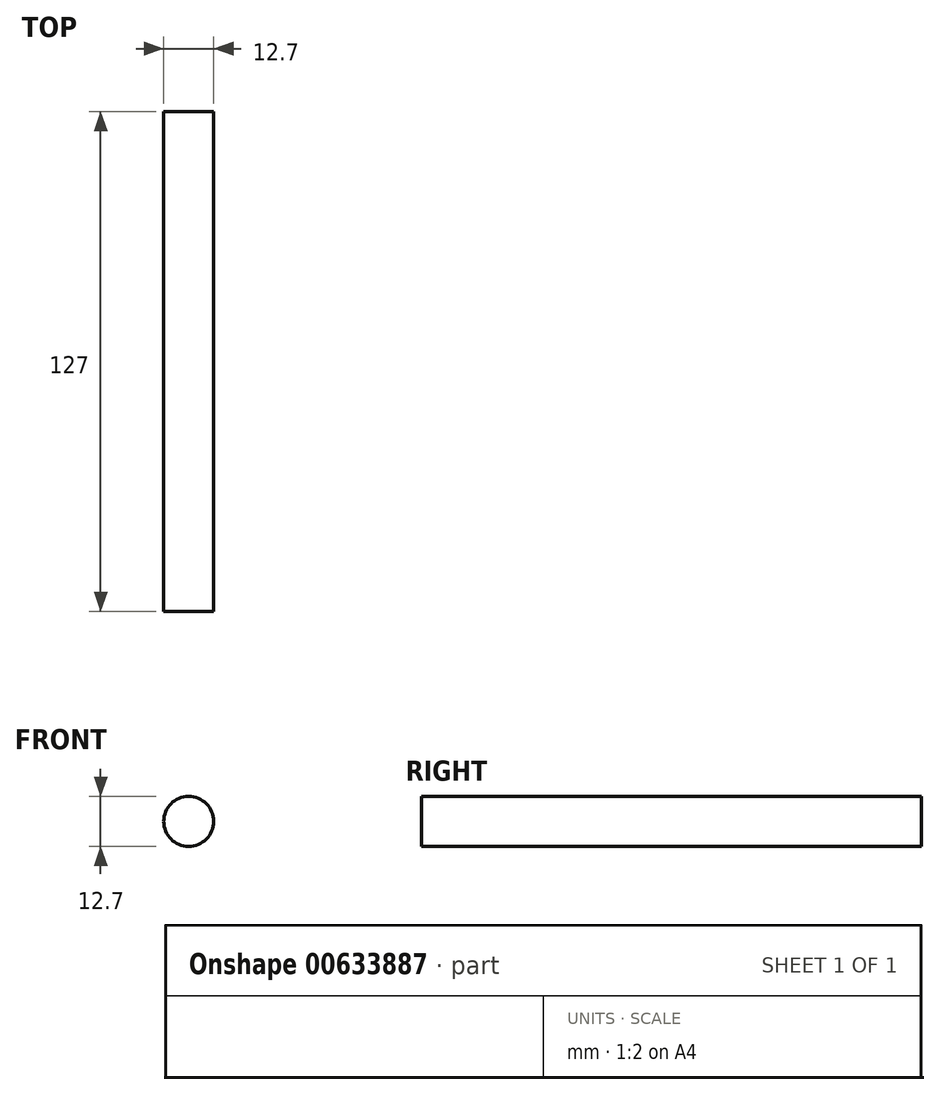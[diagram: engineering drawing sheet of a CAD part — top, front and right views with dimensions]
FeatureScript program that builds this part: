
annotation { "Feature Type Name" : "Feature", "Feature Type Description" : "" }
export const myFeature = defineFeature(function(context is Context, id is Id, definition is map)
    precondition{}
    {
        {
            var Q0;
            Q0=qCreatedBy(makeId("Front.planeOp"),FACE);
            var sketch = newSketch(context, id + "F0", { "sketchPlane" : qUnion([Q0])});
            skCircle(sketch, "E0", {"center": v(0, 0) * mm, "radius": 6.35 * mm});
            skSolve(sketch);
        }
        {
            var Q0;
            Q0=makeQuery(id+"F0.imprint","IMPRINT",FACE,{"disambiguationData":[TD([[makeQuery(id+"F0.imprint","IMPRINT",EDGE,{"derivedFrom":sQuery(id+"F0.wireOp",EDGE,"E0")}),1.0]])]});
            extrude(context, id + "F1", {"entities" : qUnion([Q0]), "depth" : 127 * mm, "offsetDistance" : 25.4 * mm});
        }
    });
